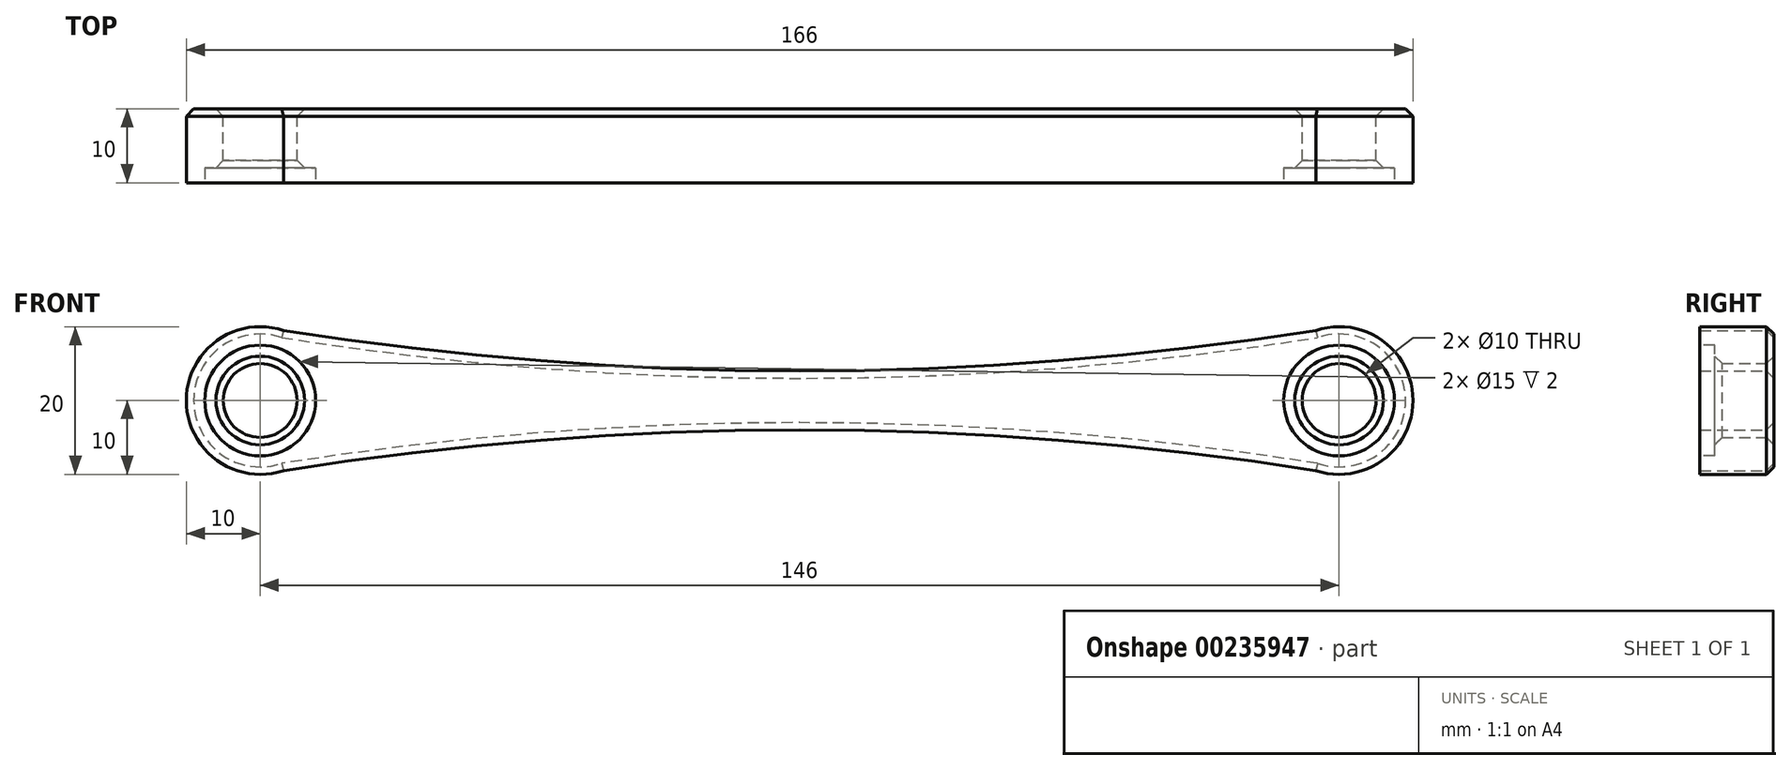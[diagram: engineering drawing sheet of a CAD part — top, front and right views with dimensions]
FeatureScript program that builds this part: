
annotation { "Feature Type Name" : "Feature", "Feature Type Description" : "" }
export const myFeature = defineFeature(function(context is Context, id is Id, definition is map)
    precondition{}
    {
        {
            var Q0;
            Q0=qCreatedBy(makeId("Front.planeOp"),FACE);
            var sketch = newSketch(context, id + "F0", { "sketchPlane" : qUnion([Q0])});
            skLineSegment(sketch, "E0", {"start": v(0, 0) * mm, "end": v(146, 0) * mm, "construction": true});
            skCircle(sketch, "E1", {"center": v(0, 0) * mm, "radius": 10 * mm});
            skCircle(sketch, "E2", {"center": v(146, 0) * mm, "radius": 10 * mm});
            skLineSegment(sketch, "E3", {"start": v(73, 0) * mm, "end": v(73, 4) * mm, "construction": true});
            skLineSegment(sketch, "E4", {"start": v(73, 0) * mm, "end": v(73, -4) * mm, "construction": true});
            skArc(sketch, "E5", {"start": v(146, -10) * mm, "mid": v(73, -4) * mm, "end": v(0, -10) * mm});
            skArc(sketch, "E6", {"start": v(0, 10) * mm, "mid": v(73, 4) * mm, "end": v(146, 10) * mm});
            skCircle(sketch, "E7", {"center": v(0, 0) * mm, "radius": 5 * mm});
            skCircle(sketch, "E8", {"center": v(146, 0) * mm, "radius": 5 * mm});
            skSolve(sketch);
        }
        {
            var Q0;
            Q0 = qSketchRegion(id + "F0", true);
            extrude(context, id + "F1", {"entities" : qUnion([Q0]), "depth" : 10 * mm});
        }
        {
            var Q0;
            Q0=makeQuery(id+"F1.opExtrude","CAP_FACE",FACE,{"disambiguationData":[OSD([sQuery(id+"F0.wireOp",EDGE,"E1"),sQuery(id+"F0.wireOp",EDGE,"E2"),sQuery(id+"F0.wireOp",EDGE,"E5"),sQuery(id+"F0.wireOp",EDGE,"E6"),sQuery(id+"F0.wireOp",EDGE,"E7"),sQuery(id+"F0.wireOp",EDGE,"E8")])],"isStart":false});
            var sketch = newSketch(context, id + "F2", { "sketchPlane" : qUnion([Q0])});
            skCircle(sketch, "E9", {"center": v(0, 0) * mm, "radius": 7.5 * mm});
            skCircle(sketch, "E10", {"center": v(146, 0) * mm, "radius": 7.5 * mm});
            skSolve(sketch);
        }
        {
            var Q0;
            Q0 = qSketchRegion(id + "F2", true);
            extrude(context, id + "F3", {"entities" : qUnion([Q0]), "operationType" : NewBodyOperationType.REMOVE, "oppositeDirection" : true, "depth" : 2 * mm});
        }
        {
            var Q0;
            Q0=makeQuery(id+"F1.opExtrude","CAP_FACE",FACE,{"disambiguationData":[OSD([sQuery(id+"F0.wireOp",EDGE,"E1"),sQuery(id+"F0.wireOp",EDGE,"E2"),sQuery(id+"F0.wireOp",EDGE,"E5"),sQuery(id+"F0.wireOp",EDGE,"E6"),sQuery(id+"F0.wireOp",EDGE,"E7"),sQuery(id+"F0.wireOp",EDGE,"E8")])],"isStart":true});
            var Q1;
            Q1=makeQuery(id+"F3.boolean.opBoolean","INTERSECT",EDGE,{"derivedFrom":[makeQuery(id+"F1.opExtrude","SWEPT_FACE",FACE,{"disambiguationData":[OSD([sQuery(id+"F0.wireOp",EDGE,"E8")])]}),makeQuery(id+"F3.opExtrude","CAP_FACE",FACE,{"disambiguationData":[OSD([sQuery(id+"F2.wireOp",EDGE,"E10")])],"isStart":false})]});
            var Q2;
            Q2=makeQuery(id+"F3.boolean.opBoolean","INTERSECT",EDGE,{"derivedFrom":[makeQuery(id+"F1.opExtrude","SWEPT_FACE",FACE,{"disambiguationData":[OSD([sQuery(id+"F0.wireOp",EDGE,"E7")])]}),makeQuery(id+"F3.opExtrude","CAP_FACE",FACE,{"disambiguationData":[OSD([sQuery(id+"F2.wireOp",EDGE,"E9")])],"isStart":false})]});
            chamfer(context, id + "F4", {"entities" : qUnion([Q0, Q1, Q2]), "width" : 1 * mm, "tangentPropagation" : true});
        }
    });
